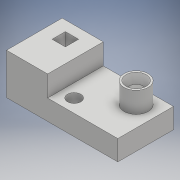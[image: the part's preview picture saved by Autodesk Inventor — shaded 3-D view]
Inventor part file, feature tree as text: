
AUTODESK INVENTOR PART (.ipt)
format: ipt  version: 2018 (Build 220112000, 112)  size: 135,680 bytes
history: native  units: mm
features: extrude x3, sketch x1, chamfer x1
ambient origin geometry x8: Origin, YZ Plane, XZ Plane, XY Plane, X Axis, Y Axis, Z Axis, Center Point
bodies: Solid1 (feature_tree)
feature tree (5):
  sketch  "Sketch1"  dims[d0=44.0mm d1=22.0mm d2=5.25mm d3=5.25mm d4=16.25mm d5=5.25mm d6=5.25mm d7=5.25mm d8=4.0mm d9=5.25mm d10=6.75mm d11=8.0mm d12=5.25mm d13=8.0mm d14=9.5mm d15=8.0mm d16=0.0mm d17=16.25mm d18=0.0mm d19=13.0mm d20=0.0mm d21=3.25mm d22=1.25mm d23=45.0deg]
  extrude  "Extrusion1"  Depth=22.0mm
  extrude  "Extrusion2"  Depth=5.25mm
  extrude  "Extrusion3"  Depth=5.25mm
  chamfer  "Chamfer1"  Distance=16.25mm
